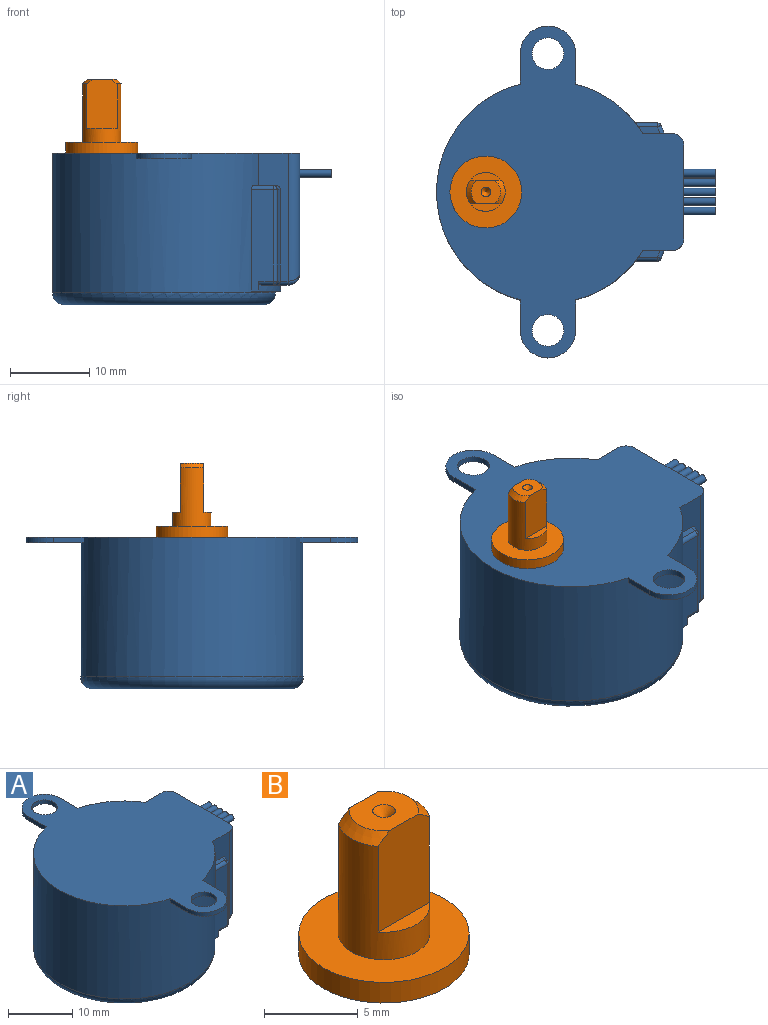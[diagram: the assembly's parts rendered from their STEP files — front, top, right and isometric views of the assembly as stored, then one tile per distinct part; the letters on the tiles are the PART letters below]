
ASSEMBLY  parts=2 mates=1
PART A: 66 faces, bbox 36.5x42x19.2 mm
  f0: cylinder r=0.5mm len=5mm, axis (-1,0,0), area 15.7mm2, adj f1,f57
  f1: plane 1x1mm, normal (1,0,0), area 0.8mm2, adj f0
  f2: plane 15.2x11.8mm, normal (1,0,0), area 169.8mm2, adj f16,f31,f32,f33,f53,f54,f55,f56
  f3: cylinder r=14.1mm len=28.2mm, axis (0,0,1), area 1244mm2, adj f4,f5,f6,f7,f8,f9,f10,f15
  f4: plane 16.5x3.36mm, normal (0,0,-1), area 25.3mm2, adj f3,f25,f26,f28,f29,f32,f39,f41
  f5: plane 16.2x3.7mm, normal (0,1,0), area 27.3mm2, adj f3,f16,f19,f20,f31,f35,f42
  f6: plane 3.84x0.75mm, normal (-1,0,0), area 2.9mm2, adj f3,f12,f15,f16
  f7: plane 3.84x0.75mm, normal (-1,0,0), area 2.9mm2, adj f3,f10,f11,f16
  f8: plane 3.84x0.75mm, normal (1,0,0), area 2.9mm2, adj f3,f12,f15,f16
  f9: plane 3.84x0.75mm, normal (1,0,0), area 2.9mm2, adj f3,f10,f11,f16
  f10: plane 7.34x7mm, normal (0,0,-1), area 31.5mm2, adj f3,f7,f9,f11,f14
  f11: cylinder r=3.5mm len=7mm, axis (0,0,1), area 8.2mm2, adj f7,f9,f10,f16
  f12: cylinder r=3.5mm len=7mm, axis (0,0,1), area 8.2mm2, adj f6,f8,f15,f16
  f13: cylinder r=2mm len=4mm, axis (0,0,1), area 9.4mm2, adj f15,f16
  f14: cylinder r=2mm len=4mm, axis (0,0,1), area 9.4mm2, adj f10,f16
  f15: plane 7.34x7mm, normal (0,0,-1), area 31.5mm2, adj f3,f6,f8,f12,f13
  f16: plane 42x31.3mm, normal (0,0,1), area 742.5mm2, adj f2,f3,f5,f6,f7,f8,f9,f11
  f17: plane 25.2x25.2mm, normal (0,0,-1), area 498.8mm2, adj f34
  f18: plane 16.2x3.7mm, normal (0,-1,0), area 27.3mm2, adj f3,f16,f22,f23,f33,f45,f51
  f19: plane 2.73x0.85mm, normal (0,0,1), area 1.9mm2, adj f3,f5,f35,f36
  f20: plane 11.6x1.02mm, normal (0.94,0.35,0), area 12.7mm2, adj f5,f35,f38,f41
  f21: plane 12.85x2.8mm, normal (0,1,0), area 33.6mm2, adj f3,f26,f27,f36,f38,f39
  f22: plane 2.73x0.85mm, normal (0,0,1), area 1.9mm2, adj f3,f18,f44,f45
  f23: plane 11.6x1.02mm, normal (0.94,-0.35,0), area 12.7mm2, adj f18,f45,f48,f50
  f24: plane 12.85x2.8mm, normal (0,-1,0), area 33.6mm2, adj f3,f28,f30,f44,f47,f48
  f25: plane 0.75x0.75mm, normal (0,-1,0), area 0.6mm2, adj f3,f4,f26,f27
  f26: cylinder r=14.85mm len=7.25mm, axis (0,0,1), area 6mm2, adj f4,f21,f25,f27,f39
  f27: plane 7.25x3.71mm, normal (0,0,-1), area 5.9mm2, adj f3,f21,f25,f26
  f28: cylinder r=14.85mm len=7.25mm, axis (0,0,1), area 6mm2, adj f4,f24,f29,f30,f47
  f29: plane 0.75x0.75mm, normal (0,1,0), area 0.6mm2, adj f3,f4,f28,f30
  f30: plane 7.25x3.71mm, normal (0,0,-1), area 5.9mm2, adj f3,f24,f28,f29
  f31: cylinder r=1.5mm len=16.2mm, axis (0,0,-1), area 37.3mm2, adj f2,f5,f16,f43
  f32: cylinder r=1.5mm len=13.8mm, axis (0,-1,0), area 30.8mm2, adj f2,f4,f43,f52
  f33: cylinder r=1.5mm len=16.2mm, axis (0,0,1), area 37.3mm2, adj f2,f16,f18,f52
  f34: torus R=12.6mm, axis (0,0,-1), area 200.7mm2, adj f3,f17
  f35: cylinder r=0.5mm len=1.2mm, axis (-0.35,0.94,0), area 0.8mm2, adj f5,f19,f20,f37
  f36: cylinder r=0.5mm len=2.8mm, axis (-1,0,0), area 2.1mm2, adj f3,f19,f21,f37
  f37: sphere r=0.5mm, area 0.3mm2, adj f35,f36,f38
  f38: cylinder r=0.5mm len=11.6mm, axis (0,0,-1), area 7.1mm2, adj f20,f21,f37,f40
  f39: cylinder r=0.5mm len=1.86mm, axis (-1,0,0), area 1.4mm2, adj f4,f21,f26,f40
  f40: sphere r=0.5mm, area 0.3mm2, adj f38,f39,f41
  f41: cylinder r=0.5mm len=1.52mm, axis (-0.35,0.94,0), area 1mm2, adj f4,f20,f40,f42
  f42: cylinder r=0.5mm len=1.35mm, axis (1,0,0), area 0.9mm2, adj f4,f5,f41,f43
  f43: bspline ~1.76x1.5mm, area 1.3mm2, adj f31,f32,f42
  f44: cylinder r=0.5mm len=2.8mm, axis (1,0,0), area 2.1mm2, adj f3,f22,f24,f46
  f45: cylinder r=0.5mm len=1.2mm, axis (0.35,0.94,0), area 0.8mm2, adj f18,f22,f23,f46
  f46: sphere r=0.5mm, area 0.3mm2, adj f44,f45,f48
  f47: cylinder r=0.5mm len=1.86mm, axis (1,0,0), area 1.4mm2, adj f4,f24,f28,f49
  f48: cylinder r=0.5mm len=11.6mm, axis (0,0,-1), area 7.1mm2, adj f23,f24,f46,f49
  f49: sphere r=0.5mm, area 0.3mm2, adj f47,f48,f50
  f50: cylinder r=0.5mm len=1.52mm, axis (0.35,0.94,0), area 1mm2, adj f4,f23,f49,f51
  f51: cylinder r=0.5mm len=1.35mm, axis (-1,0,0), area 0.9mm2, adj f4,f18,f50,f52
  f52: bspline ~1.76x1.5mm, area 1.3mm2, adj f32,f33,f51
  f53: plane 6.3x1mm, normal (0,0,1), area 6.3mm2, adj f2,f54,f56,f57
  f54: cylinder r=0.65mm len=1.3mm, axis (1,0,0), area 2mm2, adj f2,f53,f55,f57
  f55: plane 6.3x1mm, normal (0,0,-1), area 6.3mm2, adj f2,f54,f56,f57
  f56: cylinder r=0.65mm len=1.3mm, axis (1,0,0), area 2mm2, adj f2,f53,f55,f57
  f57: plane 7.6x1.3mm, normal (1,0,0), area 5.6mm2, adj f0,f53,f54,f55,f56,f58,f60,f62
  f58: cylinder r=0.5mm len=5mm, axis (-1,0,0), area 15.7mm2, adj f57,f59
  f59: plane 1x1mm, normal (1,0,0), area 0.8mm2, adj f58
  f60: cylinder r=0.5mm len=5mm, axis (-1,0,0), area 15.7mm2, adj f57,f61
  f61: plane 1x1mm, normal (1,0,0), area 0.8mm2, adj f60
  f62: cylinder r=0.5mm len=5mm, axis (-1,0,0), area 15.7mm2, adj f57,f63
  f63: plane 1x1mm, normal (1,0,0), area 0.8mm2, adj f62
  f64: cylinder r=0.5mm len=5mm, axis (-1,0,0), area 15.7mm2, adj f57,f65
  f65: plane 1x1mm, normal (1,0,0), area 0.8mm2, adj f64
PART B: 12 faces, bbox 9.2x9.2x9.5 mm
  f0: cylinder r=2.45mm len=7.4mm, axis (0,0,-1), area 63.9mm2, adj f1,f2,f4,f8,f9,f10,f11
  f1: cone r=1.85mm half-angle=45deg, axis (0,0,-1), area 2.9mm2, adj f0,f3,f9,f11
  f2: cone r=1.85mm half-angle=45deg, axis (0,0,-1), area 2.9mm2, adj f0,f3,f9,f11
  f3: plane 3.7x3mm, normal (0,0,1), area 8.6mm2, adj f1,f2,f5,f9,f11
  f4: plane 9.1x9.1mm, normal (0,0,1), area 46.2mm2, adj f0,f7
  f5: cone r=0.6mm half-angle=45deg, axis (0,0,1), area 1.6mm2, adj f3
  f6: plane 9.1x9.1mm, normal (0,0,-1), area 65mm2, adj f7
  f7: cylinder r=4.55mm len=9.1mm, axis (0,0,-1), area 38.6mm2, adj f4,f6
  f8: plane 3.87x0.95mm, normal (0,0,1), area 2.6mm2, adj f0,f9
  f9: plane 6.31x3.98mm, normal (0,-1,0), area 23.5mm2, adj f0,f1,f2,f3,f8
  f10: plane 3.87x0.95mm, normal (0,0,1), area 2.6mm2, adj f0,f11
  f11: plane 6.31x3.98mm, normal (0,1,0), area 23.5mm2, adj f0,f1,f2,f3,f10
PLACE A t=(-16.14,-4.11,12.97)mm
PLACE B t=(-16.14,-4.11,12.97)mm
MATE revolute B.f0 <-> A.f16  axis (0,0,-1) through (-16.14,-4.11,12.97)mm
